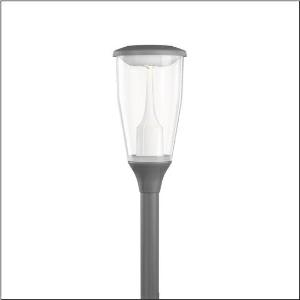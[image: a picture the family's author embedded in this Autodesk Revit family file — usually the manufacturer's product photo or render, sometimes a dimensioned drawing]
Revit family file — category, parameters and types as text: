
# Revit family: dl_11_iq___p1_0a_5xa5565ff14h000022_0ce9
name_source: partatom
category: Lighting Fixtures
units: mm (PartAtom-declared; Revit-internal decimal feet)

## family parameters
Cut with Voids When Loaded = No
Host = Face
Light Source = No
Part Type = Normal
Room Calculation Point = No
Round Connector Dimension = Use Diameter
Shared = No

## types (1)
- --- (1 x LED, 1530 lm, 10.5 W, 3000K)
    Apparent Load = 11 VA
    CIE Flux Codes = 34 63 91 95 100
    Color Rendering = 70
    Color Temperature = 3000K
    Default Elevation = 1800 mm
    Description = DL 11 iQ, mast luminaire, Module 540 iQ-SR, primary light control with 3 zone facetted reflector, of plastic, silver coated, highly specular, structured, primary optical cover: cover, of PMMA, transparent, light distribution: P1.0a, light emission: direct distribution, primary light characteristic: asymmetric, installation type: post-top, LED, High Power LED, rated luminous flux: 1.560lm, luminous efficacy: 149lm/W, light colour: 730, colour temperature: 3000K, control: Street-Remote, Auto-Match, Temp-Guard, Lumen-Switch, Night-Set, Smart-Wire, Light-Fading, Desk-Remote (wireless, voltage-free reading and setting of iQ features in the workshop via application-optimized NFC function/RFID function), optimised constant luminous flux control (CLO 2.0), mains connection: 220..240V, AC, 50/60Hz, connection cable pre-assembled, cable length: 5,5m, start of lifetime: 10W, end of service life: 11W, reduction: 5W, luminaire housing, upper part, of diecast aluminium, coated, Siteco® metallic grey (DB 702S), spigot size: 60mm (post-top), post-top mast mounting element, of diecast aluminium, coated, Siteco® metallic grey (DB 702S), Module 540 iQ-SR, traffic white (RAL 9016), equipment: standard, protection rating (complete): IP66, insulation class (complete): insulation class II (safety insulation), certification: CE, ENEC, ENEC+, VDE, packaging unit: 1 piece

Light Distribution: P1.0a
    Height = 665 mm
    Lamp = 1 x LED
    Lamp Light Flux = 1530 lm
    Lamp Power = 10.5 W
    Lamp count = 1
    Length = 334 mm
    Luminous efficacy = 146 lm/W
    Manufacturer = Siteco
    ModVariant = No
    Model = 5XA5565FF14H000022
    Number of Poles = 1
    OnlyDefault = Yes
    Power Factor = 1
    Product Name = DL 11 iQ | P1.0a
    Product group = mast luminaire | pylon top
    ProductGroupID = 6100
    Protection Class = Protection class II
    Protection Degree = IP 66
    RLX_Detail_Level = 1
    RLX_Emergency_Light_Flux = 0 lm
    RLX_Emergency_Type = 0
    RLX_Emergency_Type_DB = No
    RlxData = <blob elided: 103593 chars, md5=2b2d62d5>
    Socket = socket
    Standby Power = 0 W
    System Light Flux = 1530 lm
    System Power = 11 W
    Type Comments = factory setting: luminous flux: 100 % | dim-lin: 254 | 419 mA
    Type Image = l_1258354.jpg
    URL = http://relux.com
    VarID = @adj_060665
    Voltage = 0 V
    Weight = 0.00 kg
    Width = 0 mm  [stored 0 ft]

note: [stored X ft] marks values corroborated as IEEE doubles in the binary element streams (Revit-internal decimal feet)

## geometry (parser evidence)
native form markers: Blend x4, Sweep x12
no freeform markers — native parametric forms only
